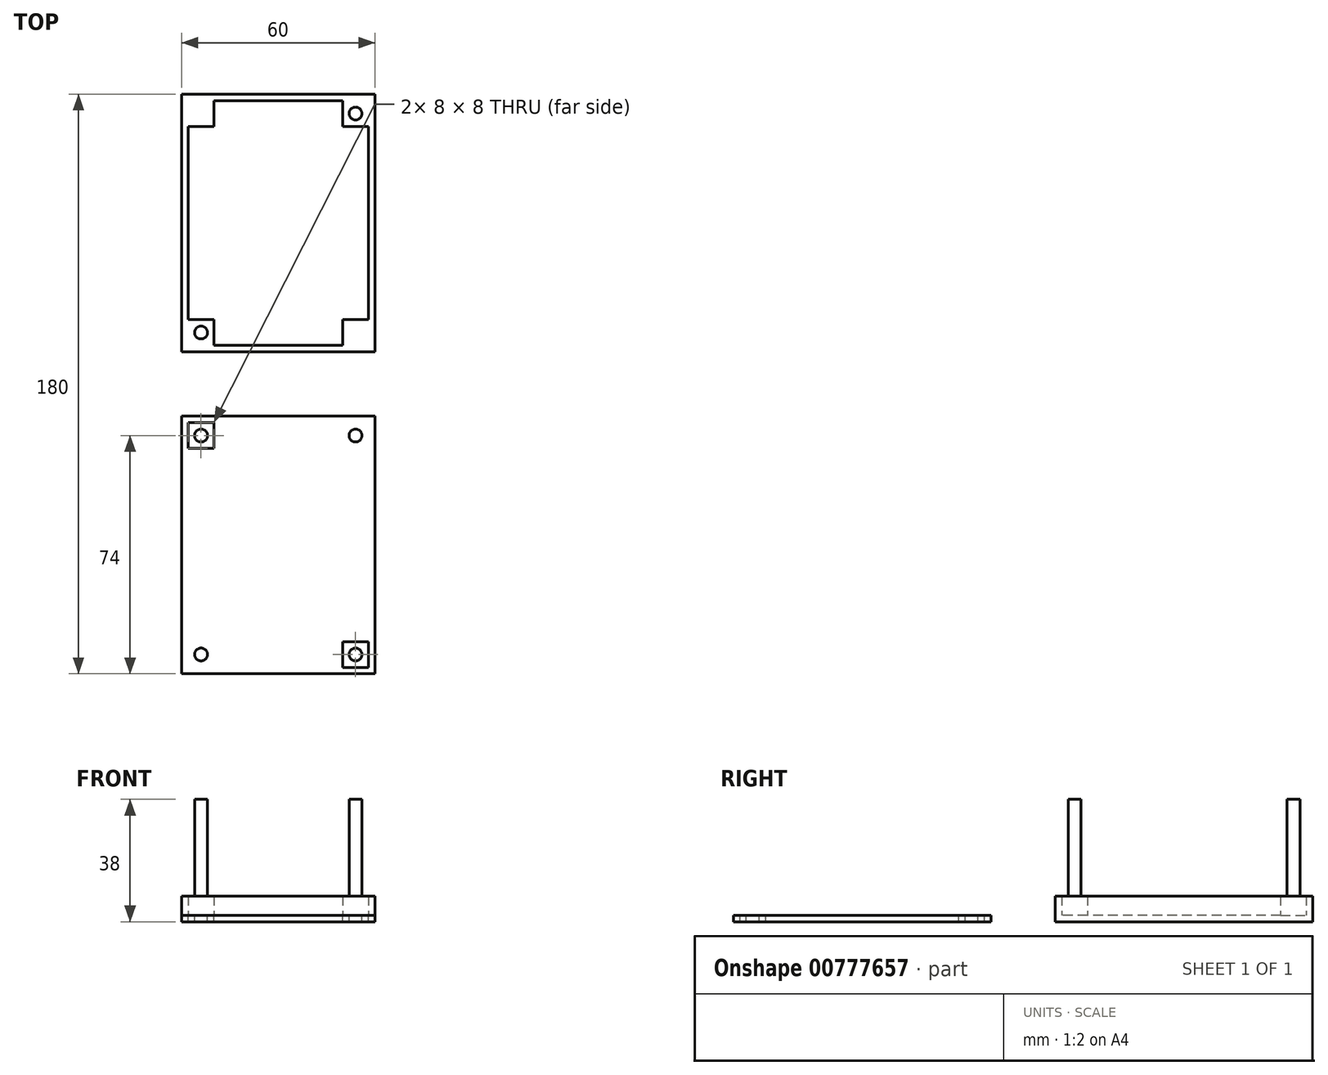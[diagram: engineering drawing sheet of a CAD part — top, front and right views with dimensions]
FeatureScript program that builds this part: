
annotation { "Feature Type Name" : "Feature", "Feature Type Description" : "" }
export const myFeature = defineFeature(function(context is Context, id is Id, definition is map)
    precondition{}
    {
        {
            assignVariable(context, id + "F0", {"name" : "height", "anyValue" : 40});
        }
        {
            assignVariable(context, id + "F1", {"name" : "wallThickness", "anyValue" : 2});
        }
        {
            assignVariable(context, id + "F2", {"name" : "drillHoleDepth", "anyValue" : getVariable(context, 'height') / 4 * 3});
        }
        {
            var Q0;
            Q0=qCreatedBy(makeId("Top.planeOp"),FACE);
            var sketch = newSketch(context, id + "F3", { "sketchPlane" : qUnion([Q0])});
            skLineSegment(sketch, "E0.bottom", {"start": v(-30, -40) * mm, "end": v(30, -40) * mm});
            skLineSegment(sketch, "E0.top", {"start": v(-30, 40) * mm, "end": v(30, 40) * mm});
            skLineSegment(sketch, "E0.left", {"start": v(-30, -40) * mm, "end": v(-30, 40) * mm});
            skLineSegment(sketch, "E0.right", {"start": v(30, -40) * mm, "end": v(30, 40) * mm});
            skPoint(sketch, "E0.middle", {"position": v(0, 0) * mm});
            skSolve(sketch);
        }
        {
            var Q0;
            Q0=makeQuery(id+"F3.imprint","IMPRINT",FACE,{"disambiguationData":[TD([[makeQuery(id+"F3.imprint","IMPRINT",EDGE,{"derivedFrom":sQuery(id+"F3.wireOp",EDGE,"E0.bottom")}),1.0]])]});
            extrude(context, id + "F4", {"entities" : qUnion([Q0]), "depth" : (getVariable(context, 'height') - getVariable(context, 'wallThickness')) * mm, "offsetDistance" : 25 * mm});
        }
        {
            var Q0;
            Q0=makeQuery(id+"F4.opExtrude","CAP_FACE",FACE,{"disambiguationData":[OSD([sQuery(id+"F3.wireOp",EDGE,"E0.bottom"),sQuery(id+"F3.wireOp",EDGE,"E0.top"),sQuery(id+"F3.wireOp",EDGE,"E0.left"),sQuery(id+"F3.wireOp",EDGE,"E0.right")])],"isStart":false});
            var sketch = newSketch(context, id + "F5", { "sketchPlane" : qUnion([Q0])});
            skLineSegment(sketch, "E1.bottom", {"start": v(-28, 38) * mm, "end": v(28, 38) * mm});
            skLineSegment(sketch, "E1.top", {"start": v(-28, -38) * mm, "end": v(28, -38) * mm});
            skLineSegment(sketch, "E1.left", {"start": v(-28, 38) * mm, "end": v(-28, -38) * mm});
            skLineSegment(sketch, "E1.right", {"start": v(28, 38) * mm, "end": v(28, -38) * mm});
            skPoint(sketch, "E1.middle", {"position": v(0, 0) * mm});
            skSolve(sketch);
        }
        {
            var Q0;
            Q0=makeQuery(id+"F5.imprint","IMPRINT",FACE,{"disambiguationData":[TD([[makeQuery(id+"F5.imprint","IMPRINT",EDGE,{"derivedFrom":sQuery(id+"F5.wireOp",EDGE,"E1.bottom")}),-1.0]])]});
            extrude(context, id + "F6", {"entities" : qUnion([Q0]), "operationType" : NewBodyOperationType.REMOVE, "oppositeDirection" : true, "depth" : (getVariable(context, 'height') - (getVariable(context, 'wallThickness') * 2)) * mm, "offsetDistance" : 25 * mm});
        }
        {
            var Q0;
            Q0=makeQuery(id+"F6.boolean.opBoolean","COPY",FACE,{"derivedFrom":makeQuery(id+"F6.opExtrude","CAP_FACE",FACE,{"disambiguationData":[OSD([sQuery(id+"F5.wireOp",EDGE,"E1.bottom"),sQuery(id+"F5.wireOp",EDGE,"E1.top"),sQuery(id+"F5.wireOp",EDGE,"E1.left"),sQuery(id+"F5.wireOp",EDGE,"E1.right")])],"isStart":false})});
            var sketch = newSketch(context, id + "F7", { "sketchPlane" : qUnion([Q0])});
            skLineSegment(sketch, "E2.bottom", {"start": v(-28, -30) * mm, "end": v(-20, -30) * mm});
            skLineSegment(sketch, "E2.top", {"start": v(-28, -38) * mm, "end": v(-20, -38) * mm});
            skLineSegment(sketch, "E2.left", {"start": v(-28, -30) * mm, "end": v(-28, -38) * mm});
            skLineSegment(sketch, "E2.right", {"start": v(-20, -30) * mm, "end": v(-20, -38) * mm});
            skLineSegment(sketch, "E3", {"start": v(0, 38) * mm, "end": v(0, -38) * mm, "construction": true});
            skLineSegment(sketch, "E4", {"start": v(-28, 0) * mm, "end": v(28, 0) * mm, "construction": true});
            skLineSegment(sketch, "E5.MirrorCS", {"start": v(-20, 30) * mm, "end": v(-20, 38) * mm});
            skLineSegment(sketch, "E6.MirrorCS", {"start": v(-28, 30) * mm, "end": v(-28, 38) * mm});
            skLineSegment(sketch, "E7.MirrorCS", {"start": v(-28, 38) * mm, "end": v(-20, 38) * mm});
            skLineSegment(sketch, "E8.MirrorCS", {"start": v(-28, 30) * mm, "end": v(-20, 30) * mm});
            skLineSegment(sketch, "E9.MirrorCS", {"start": v(28, 30) * mm, "end": v(28, 38) * mm});
            skLineSegment(sketch, "E10.MirrorCS", {"start": v(28, -30) * mm, "end": v(20, -30) * mm});
            skLineSegment(sketch, "E11.MirrorCS", {"start": v(28, -30) * mm, "end": v(28, -38) * mm});
            skLineSegment(sketch, "E12.MirrorCS", {"start": v(20, -30) * mm, "end": v(20, -38) * mm});
            skLineSegment(sketch, "E13.MirrorCS", {"start": v(28, 0) * mm, "end": v(-28, 0) * mm, "construction": true});
            skLineSegment(sketch, "E14.MirrorCS", {"start": v(20, 30) * mm, "end": v(20, 38) * mm});
            skLineSegment(sketch, "E15.MirrorCS", {"start": v(28, 38) * mm, "end": v(20, 38) * mm});
            skLineSegment(sketch, "E16.MirrorCS", {"start": v(28, -38) * mm, "end": v(20, -38) * mm});
            skLineSegment(sketch, "E17.MirrorCS", {"start": v(28, 30) * mm, "end": v(20, 30) * mm});
            skSolve(sketch);
        }
        {
            var Q0;
            Q0=makeQuery(id+"F7.imprint","IMPRINT",FACE,{"disambiguationData":[TD([[makeQuery(id+"F7.imprint","IMPRINT",EDGE,{"derivedFrom":sQuery(id+"F7.wireOp",EDGE,"E5.MirrorCS")}),1.0]])]});
            var Q1;
            Q1=makeQuery(id+"F7.imprint","IMPRINT",FACE,{"disambiguationData":[TD([[makeQuery(id+"F7.imprint","IMPRINT",EDGE,{"derivedFrom":sQuery(id+"F7.wireOp",EDGE,"E9.MirrorCS")}),-1.0]])]});
            var Q2;
            Q2=makeQuery(id+"F7.imprint","IMPRINT",FACE,{"disambiguationData":[TD([[makeQuery(id+"F7.imprint","IMPRINT",EDGE,{"derivedFrom":sQuery(id+"F7.wireOp",EDGE,"E10.MirrorCS")}),1.0]])]});
            var Q3;
            Q3=makeQuery(id+"F7.imprint","IMPRINT",FACE,{"disambiguationData":[TD([[makeQuery(id+"F7.imprint","IMPRINT",EDGE,{"derivedFrom":sQuery(id+"F7.wireOp",EDGE,"E2.bottom")}),-1.0]])]});
            extrude(context, id + "F8", {"entities" : qUnion([Q0, Q1, Q2, Q3]), "operationType" : NewBodyOperationType.ADD, "depth" : (getVariable(context, 'height') - (getVariable(context, 'wallThickness') * 2)) * mm, "offsetDistance" : 25 * mm});
        }
        {
            var Q0;
            Q0=makeQuery(id+"F8.boolean.opBoolean","MERGE",FACE,{"derivedFrom":[makeQuery(id+"F4.opExtrude","CAP_FACE",FACE,{"disambiguationData":[OSD([sQuery(id+"F3.wireOp",EDGE,"E0.bottom"),sQuery(id+"F3.wireOp",EDGE,"E0.top"),sQuery(id+"F3.wireOp",EDGE,"E0.left"),sQuery(id+"F3.wireOp",EDGE,"E0.right")])],"isStart":false}),makeQuery(id+"F8.opExtrude","CAP_FACE",FACE,{"disambiguationData":[OSD([sQuery(id+"F7.wireOp",EDGE,"E2.bottom"),sQuery(id+"F7.wireOp",EDGE,"E2.top"),sQuery(id+"F7.wireOp",EDGE,"E2.left"),sQuery(id+"F7.wireOp",EDGE,"E2.right")])],"isStart":false}),makeQuery(id+"F8.opExtrude","CAP_FACE",FACE,{"disambiguationData":[OSD([sQuery(id+"F7.wireOp",EDGE,"E5.MirrorCS"),sQuery(id+"F7.wireOp",EDGE,"E6.MirrorCS"),sQuery(id+"F7.wireOp",EDGE,"E7.MirrorCS"),sQuery(id+"F7.wireOp",EDGE,"E8.MirrorCS")])],"isStart":false}),makeQuery(id+"F8.opExtrude","CAP_FACE",FACE,{"disambiguationData":[OSD([sQuery(id+"F7.wireOp",EDGE,"E9.MirrorCS"),sQuery(id+"F7.wireOp",EDGE,"E14.MirrorCS"),sQuery(id+"F7.wireOp",EDGE,"E15.MirrorCS"),sQuery(id+"F7.wireOp",EDGE,"E17.MirrorCS")])],"isStart":false}),makeQuery(id+"F8.opExtrude","CAP_FACE",FACE,{"disambiguationData":[OSD([sQuery(id+"F7.wireOp",EDGE,"E10.MirrorCS"),sQuery(id+"F7.wireOp",EDGE,"E11.MirrorCS"),sQuery(id+"F7.wireOp",EDGE,"E12.MirrorCS"),sQuery(id+"F7.wireOp",EDGE,"E16.MirrorCS")])],"isStart":false})]});
            var sketch = newSketch(context, id + "F9", { "sketchPlane" : qUnion([Q0])});
            skCircle(sketch, "E18", {"center": v(-24, 34) * mm, "radius": 2 * mm});
            skPoint(sketch, "E18.centerSnap0", {"position": v(-20, 34) * mm});
            skPoint(sketch, "E18.centerSnap1", {"position": v(-24, 30) * mm});
            skLineSegment(sketch, "E19", {"start": v(0, 40) * mm, "end": v(0, -40) * mm, "construction": true});
            skLineSegment(sketch, "E20", {"start": v(-30, 0) * mm, "end": v(30, 0) * mm, "construction": true});
            skCircle(sketch, "E21.MirrorC", {"center": v(24, 34) * mm, "radius": 2 * mm});
            skCircle(sketch, "E22.MirrorC", {"center": v(-24, -34) * mm, "radius": 2 * mm});
            skCircle(sketch, "E23.MirrorC", {"center": v(24, -34) * mm, "radius": 2 * mm});
            skSolve(sketch);
        }
        {
            var Q0;
            Q0=makeQuery(id+"F9.imprint","IMPRINT",FACE,{"disambiguationData":[TD([[makeQuery(id+"F9.imprint","IMPRINT",EDGE,{"derivedFrom":sQuery(id+"F9.wireOp",EDGE,"E18")}),1.0]])]});
            var Q1;
            Q1=makeQuery(id+"F9.imprint","IMPRINT",FACE,{"disambiguationData":[TD([[makeQuery(id+"F9.imprint","IMPRINT",EDGE,{"derivedFrom":sQuery(id+"F9.wireOp",EDGE,"E21.MirrorC")}),-1.0]])]});
            var Q2;
            Q2=makeQuery(id+"F9.imprint","IMPRINT",FACE,{"disambiguationData":[TD([[makeQuery(id+"F9.imprint","IMPRINT",EDGE,{"derivedFrom":sQuery(id+"F9.wireOp",EDGE,"E23.MirrorC")}),1.0]])]});
            var Q3;
            Q3=makeQuery(id+"F9.imprint","IMPRINT",FACE,{"disambiguationData":[TD([[makeQuery(id+"F9.imprint","IMPRINT",EDGE,{"derivedFrom":sQuery(id+"F9.wireOp",EDGE,"E22.MirrorC")}),-1.0]])]});
            extrude(context, id + "F10", {"entities" : qUnion([Q0, Q1, Q2, Q3]), "operationType" : NewBodyOperationType.REMOVE, "oppositeDirection" : true, "depth" : (getVariable(context, 'drillHoleDepth')) * mm, "offsetDistance" : 25 * mm});
        }
        {
            var Q0;
            Q0=qCreatedBy(makeId("Top.planeOp"),FACE);
            var sketch = newSketch(context, id + "F11", { "sketchPlane" : qUnion([Q0])});
            skLineSegment(sketch, "E24.bottom", {"start": v(-30, -60) * mm, "end": v(30, -60) * mm});
            skLineSegment(sketch, "E24.top", {"start": v(-30, -140) * mm, "end": v(30, -140) * mm});
            skLineSegment(sketch, "E24.left", {"start": v(-30, -60) * mm, "end": v(-30, -140) * mm});
            skLineSegment(sketch, "E24.right", {"start": v(30, -60) * mm, "end": v(30, -140) * mm});
            skSolve(sketch);
        }
        {
            var Q0;
            Q0=makeQuery(id+"F11.imprint","IMPRINT",FACE,{"disambiguationData":[TD([[makeQuery(id+"F11.imprint","IMPRINT",EDGE,{"derivedFrom":sQuery(id+"F11.wireOp",EDGE,"E24.bottom")}),-1.0]])]});
            extrude(context, id + "F12", {"entities" : qUnion([Q0]), "depth" : (getVariable(context, 'wallThickness')) * mm, "offsetDistance" : 25 * mm});
        }
        {
            var Q0;
            Q0=makeQuery(id+"F12.opExtrude","CAP_FACE",FACE,{"disambiguationData":[OSD([sQuery(id+"F11.wireOp",EDGE,"E24.bottom"),sQuery(id+"F11.wireOp",EDGE,"E24.top"),sQuery(id+"F11.wireOp",EDGE,"E24.left"),sQuery(id+"F11.wireOp",EDGE,"E24.right")])],"isStart":false});
            var sketch = newSketch(context, id + "F13", { "sketchPlane" : qUnion([Q0])});
            skLineSegment(sketch, "E25.bottom", {"start": v(-30, -140) * mm, "end": v(-20, -140) * mm});
            skLineSegment(sketch, "E25.top", {"start": v(-30, -130) * mm, "end": v(-20, -130) * mm});
            skLineSegment(sketch, "E25.left", {"start": v(-30, -140) * mm, "end": v(-30, -130) * mm});
            skLineSegment(sketch, "E25.right", {"start": v(-20, -140) * mm, "end": v(-20, -130) * mm});
            skLineSegment(sketch, "E26", {"start": v(0, -60) * mm, "end": v(0, -140) * mm, "construction": true});
            skLineSegment(sketch, "E27", {"start": v(30, -100) * mm, "end": v(-30, -100) * mm, "construction": true});
            skLineSegment(sketch, "E28.MirrorCS", {"start": v(-30, -70) * mm, "end": v(-20, -70) * mm});
            skLineSegment(sketch, "E29.MirrorCS", {"start": v(-30, -60) * mm, "end": v(-20, -60) * mm});
            skLineSegment(sketch, "E30.MirrorCS", {"start": v(-30, -60) * mm, "end": v(-30, -70) * mm});
            skLineSegment(sketch, "E31.MirrorCS", {"start": v(-20, -60) * mm, "end": v(-20, -70) * mm});
            skLineSegment(sketch, "E32.MirrorCS", {"start": v(20, -140) * mm, "end": v(20, -130) * mm});
            skLineSegment(sketch, "E33.MirrorCS", {"start": v(30, -70) * mm, "end": v(20, -70) * mm});
            skLineSegment(sketch, "E34.MirrorCS", {"start": v(30, -60) * mm, "end": v(20, -60) * mm});
            skLineSegment(sketch, "E35.MirrorCS", {"start": v(30, -140) * mm, "end": v(30, -130) * mm});
            skLineSegment(sketch, "E36.MirrorCS", {"start": v(30, -140) * mm, "end": v(20, -140) * mm});
            skLineSegment(sketch, "E37.MirrorCS", {"start": v(20, -60) * mm, "end": v(20, -70) * mm});
            skLineSegment(sketch, "E38.MirrorCS", {"start": v(30, -130) * mm, "end": v(20, -130) * mm});
            skLineSegment(sketch, "E39.MirrorCS", {"start": v(30, -60) * mm, "end": v(30, -70) * mm});
            skLineSegment(sketch, "E40.bottom", {"start": v(-20, -130) * mm, "end": v(-28, -130) * mm});
            skLineSegment(sketch, "E40.top", {"start": v(-20, -138) * mm, "end": v(-28, -138) * mm});
            skLineSegment(sketch, "E40.left", {"start": v(-20, -130) * mm, "end": v(-20, -138) * mm});
            skLineSegment(sketch, "E40.right", {"start": v(-28, -130) * mm, "end": v(-28, -138) * mm});
            skCircle(sketch, "E41", {"center": v(-24, -134) * mm, "radius": 2 * mm});
            skPoint(sketch, "E41.centerSnap0", {"position": v(-20, -134) * mm});
            skPoint(sketch, "E41.centerSnap1", {"position": v(-24, -130) * mm});
            skCircle(sketch, "E42.MirrorC", {"center": v(-24, -66) * mm, "radius": 2 * mm});
            skLineSegment(sketch, "E43.MirrorCS", {"start": v(-28, -70) * mm, "end": v(-28, -62) * mm});
            skLineSegment(sketch, "E44.MirrorCS", {"start": v(-20, -62) * mm, "end": v(-28, -62) * mm});
            skPoint(sketch, "E45.MirrorP", {"position": v(24, -130) * mm});
            skCircle(sketch, "E46.MirrorC", {"center": v(24, -134) * mm, "radius": 2 * mm});
            skLineSegment(sketch, "E47.MirrorCS", {"start": v(28, -130) * mm, "end": v(28, -138) * mm});
            skLineSegment(sketch, "E48.MirrorCS", {"start": v(20, -138) * mm, "end": v(28, -138) * mm});
            skLineSegment(sketch, "E49.MirrorCS", {"start": v(28, -70) * mm, "end": v(28, -62) * mm});
            skLineSegment(sketch, "E50.MirrorCS", {"start": v(20, -62) * mm, "end": v(28, -62) * mm});
            skCircle(sketch, "E51.MirrorC", {"center": v(24, -66) * mm, "radius": 2 * mm});
            skSolve(sketch);
        }
        {
            var Q0;
            Q0=makeQuery(id+"F13.imprint","IMPRINT",FACE,{"disambiguationData":[TD([[makeQuery(id+"F13.imprint","IMPRINT",EDGE,{"derivedFrom":sQuery(id+"F13.wireOp",EDGE,"E41")}),1.0]])]});
            var Q1;
            Q1=makeQuery(id+"F13.imprint","IMPRINT",FACE,{"disambiguationData":[TD([[makeQuery(id+"F13.imprint","IMPRINT",EDGE,{"derivedFrom":sQuery(id+"F13.wireOp",EDGE,"E42.MirrorC")}),-1.0]])]});
            var Q2;
            Q2=makeQuery(id+"F13.imprint","IMPRINT",FACE,{"disambiguationData":[TD([[makeQuery(id+"F13.imprint","IMPRINT",EDGE,{"derivedFrom":sQuery(id+"F13.wireOp",EDGE,"E51.MirrorC")}),1.0]])]});
            var Q3;
            Q3=makeQuery(id+"F13.imprint","IMPRINT",FACE,{"disambiguationData":[TD([[makeQuery(id+"F13.imprint","IMPRINT",EDGE,{"derivedFrom":sQuery(id+"F13.wireOp",EDGE,"E46.MirrorC")}),-1.0]])]});
            extrude(context, id + "F14", {"entities" : qUnion([Q0, Q1, Q2, Q3]), "operationType" : NewBodyOperationType.REMOVE, "oppositeDirection" : true, "depth" : (getVariable(context, 'wallThickness')) * mm, "offsetDistance" : 25 * mm});
        }
    });
